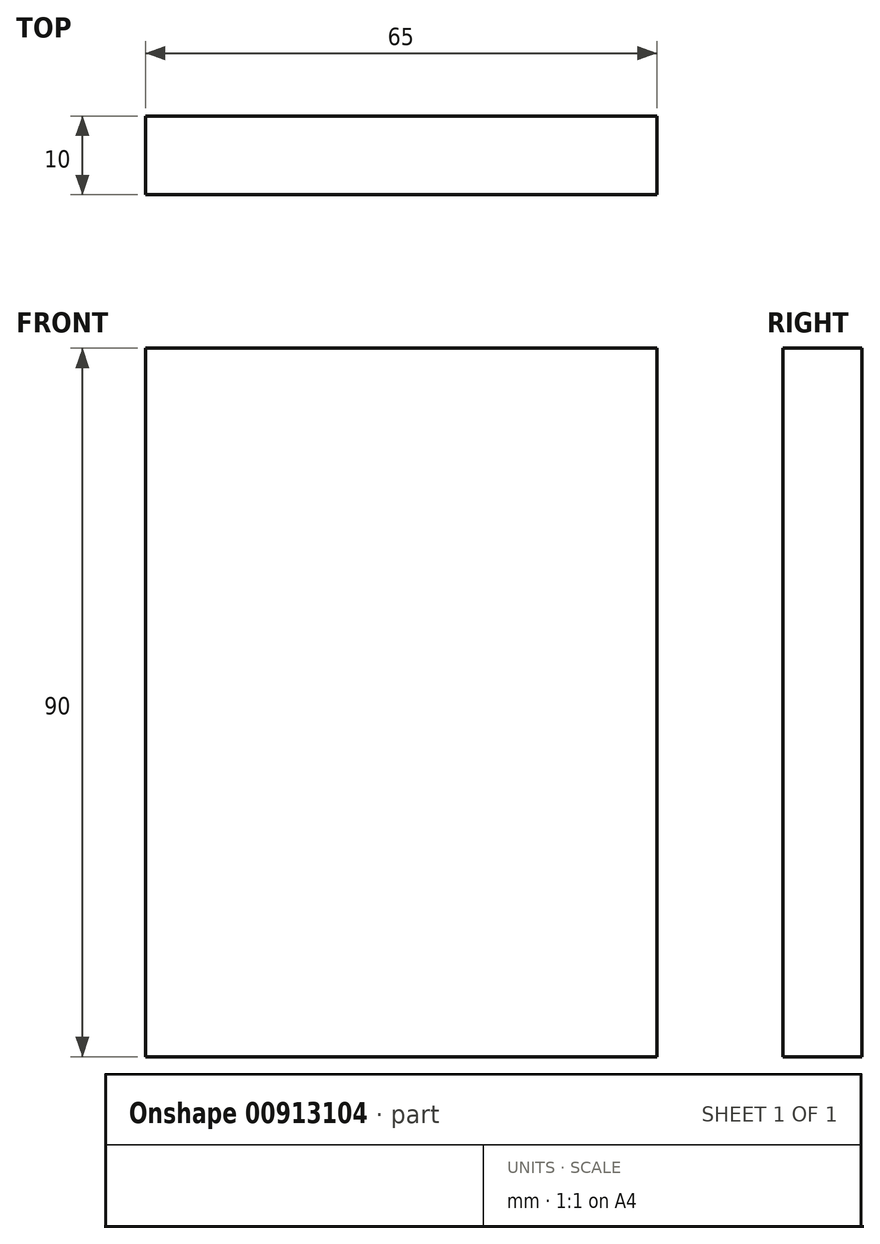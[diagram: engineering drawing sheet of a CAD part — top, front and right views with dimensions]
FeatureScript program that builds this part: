
annotation { "Feature Type Name" : "Feature", "Feature Type Description" : "" }
export const myFeature = defineFeature(function(context is Context, id is Id, definition is map)
    precondition{}
    {
        {
            var Q0;
            Q0=qCreatedBy(makeId("Front.planeOp"),FACE);
            var sketch = newSketch(context, id + "F0", { "sketchPlane" : qUnion([Q0])});
            skLineSegment(sketch, "E0.bottom", {"start": v(32.5, -45) * mm, "end": v(-32.5, -45) * mm});
            skLineSegment(sketch, "E0.top", {"start": v(32.5, 45) * mm, "end": v(-32.5, 45) * mm});
            skLineSegment(sketch, "E0.left", {"start": v(32.5, -45) * mm, "end": v(32.5, 45) * mm});
            skLineSegment(sketch, "E0.right", {"start": v(-32.5, -45) * mm, "end": v(-32.5, 45) * mm});
            skPoint(sketch, "E0.middle", {"position": v(0, 0) * mm});
            skSolve(sketch);
        }
        {
            var Q0;
            Q0 = qSketchRegion(id + "F0", true);
            extrude(context, id + "F1", {"entities" : qUnion([Q0]), "depth" : 10 * mm, "offsetDistance" : 25 * mm});
        }
    });
